# Revit family: Haworth_ActiveComponents_StorageNook_DualSideOpen_NEW
name_source: partatom
category: Furniture Systems
revit_build: Autodesk Revit Architecture 2015 (Build: 20141119_1515(x64)
units: mm (PartAtom-declared; Revit-internal decimal feet)

## types (1)
- 72w 14h
    Actual Depth = 12"
    Actual Height = 14 1/4"
    Actual Width = 72"
    Assembly Code = E2020200
    Custom Size = No
    Description = Haworth Active Components - Storage Nook Open - Dual Sided - 72w 14h
    Manufacturer = Haworth
    Max. Width = 72"
    Min. Width = 24"
    Model = AU2A
    Mounted Height = 29"
    Panel Thickness = 1/16"
    Revision Number = 2
    Size = Verify Final Dim. w/ Haworth
    Slot Length = 20"
    Stanchion Height = 4 3/8"
    Support Post Overall Width = 46"
    Support Post Width = 2"
    Sustainability Info = https://www.haworth.com
    URL = http://www.haworth.com
    URL - Product = http://www.haworth.com
    Void Side Dimension = 20"
    Warranty = https://www.haworth.com
    Width = 72"
    With Slots = Yes

## geometry (parser evidence)
native form markers: Sweep x5
no freeform markers — native parametric forms only
